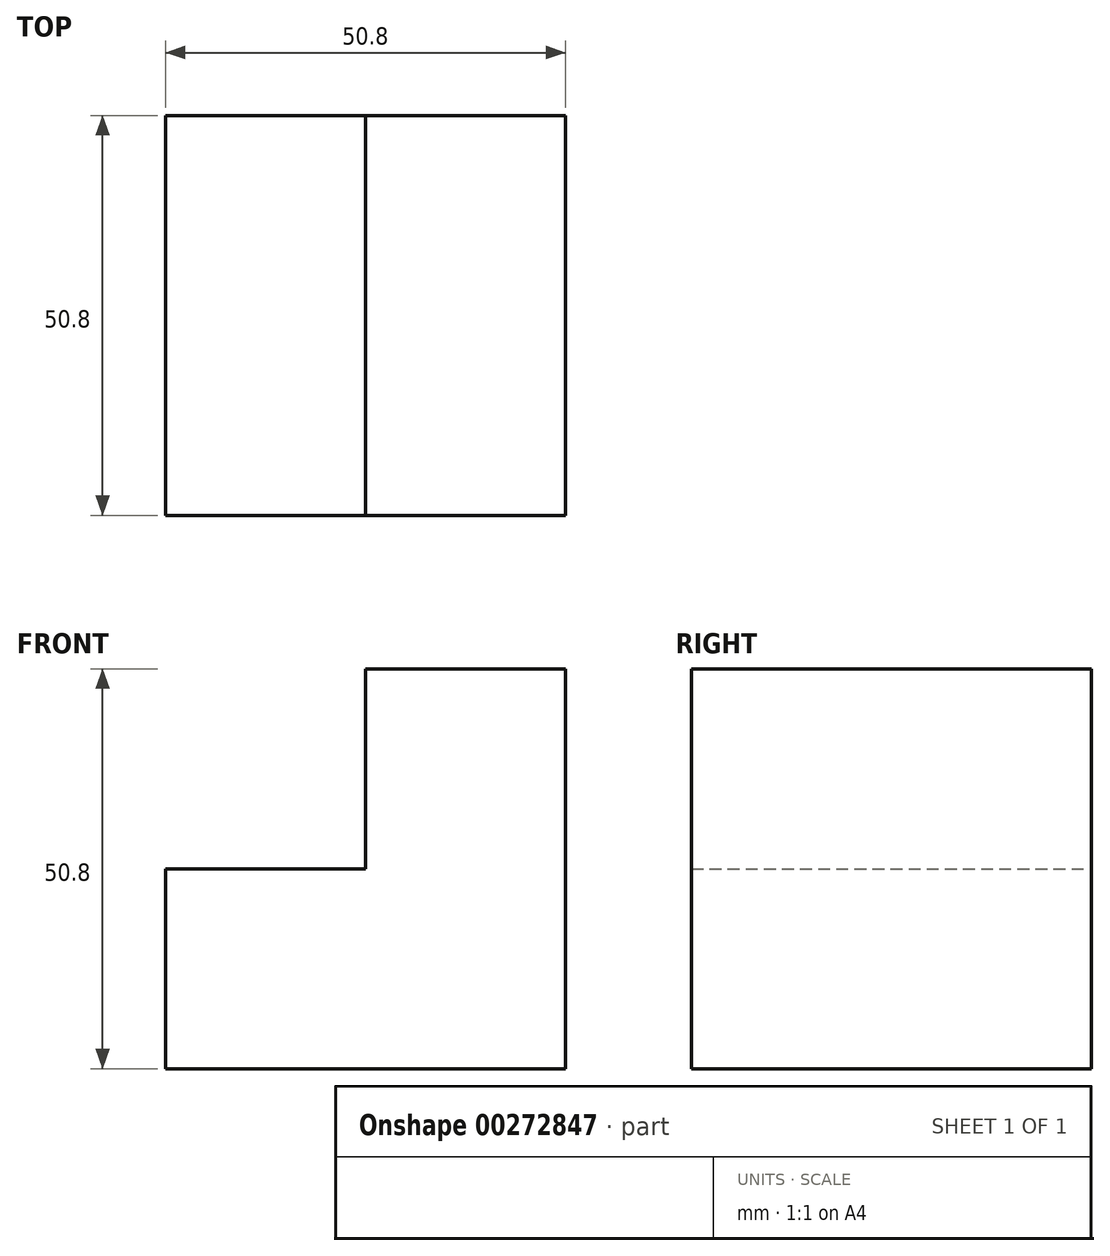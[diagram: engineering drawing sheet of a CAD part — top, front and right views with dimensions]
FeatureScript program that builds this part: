
annotation { "Feature Type Name" : "Feature", "Feature Type Description" : "" }
export const myFeature = defineFeature(function(context is Context, id is Id, definition is map)
    precondition{}
    {
        {
            var Q0;
            Q0=qCreatedBy(makeId("Front.planeOp"),FACE);
            var sketch = newSketch(context, id + "F0", { "sketchPlane" : qUnion([Q0])});
            skLineSegment(sketch, "E0", {"start": v(0, 0) * mm, "end": v(0, 50.8) * mm});
            skLineSegment(sketch, "E1", {"start": v(0, 0) * mm, "end": v(-50.8, 0) * mm});
            skLineSegment(sketch, "E2", {"start": v(-50.8, 0) * mm, "end": v(-50.8, 25.4) * mm});
            skLineSegment(sketch, "E3", {"start": v(0, 50.8) * mm, "end": v(-25.4, 50.8) * mm});
            skLineSegment(sketch, "E4", {"start": v(-25.4, 50.8) * mm, "end": v(-25.4, 25.4) * mm});
            skLineSegment(sketch, "E5", {"start": v(-25.4, 25.4) * mm, "end": v(-50.8, 25.4) * mm});
            skSolve(sketch);
        }
        {
            var Q0;
            Q0 = qSketchRegion(id + "F0", true);
            extrude(context, id + "F1", {"entities" : qUnion([Q0]), "depth" : 50.8 * mm});
        }
    });
